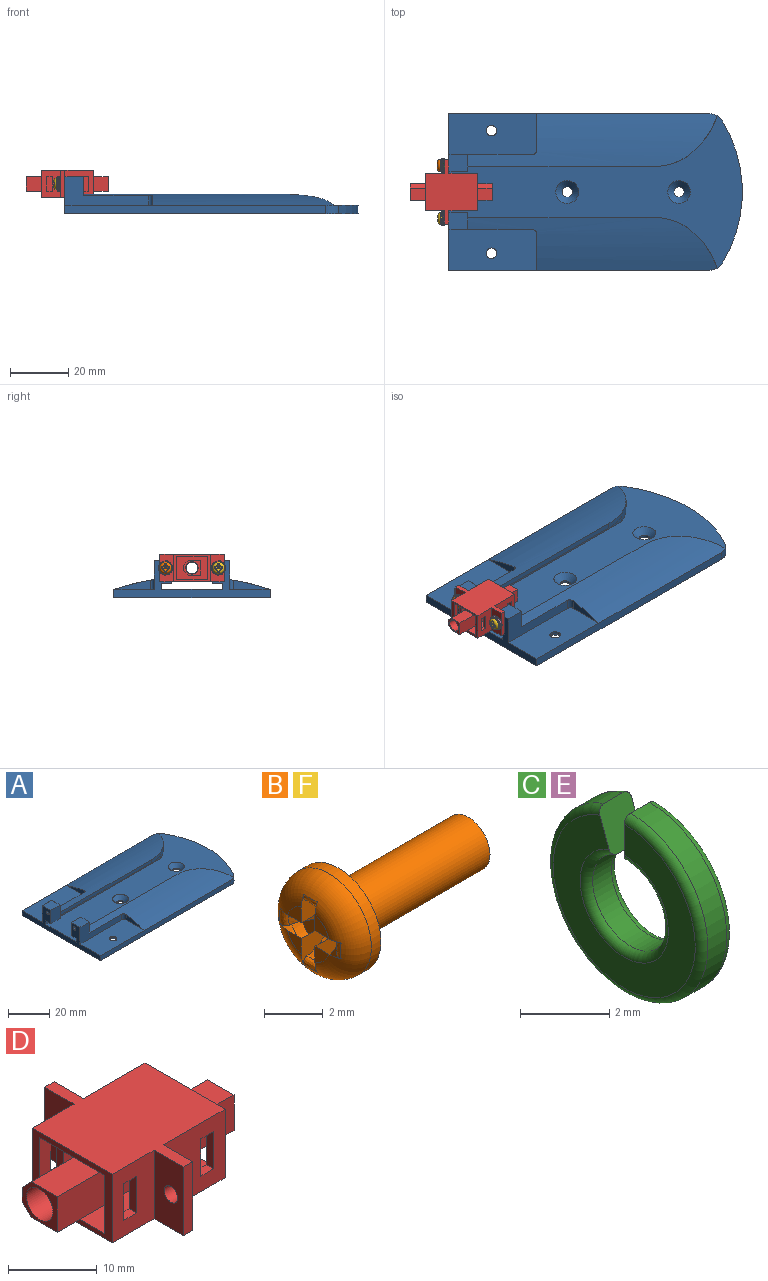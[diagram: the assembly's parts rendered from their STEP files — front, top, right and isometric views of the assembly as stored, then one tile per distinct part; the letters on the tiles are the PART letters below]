
ASSEMBLY  parts=6 mates=9
PART A: 44 faces, bbox 100.3x53.4x12.8 mm
  f0: plane 78.12x3.28mm, normal (0,0,-1), area 131mm2, adj f8,f10,f13,f15,f41,f43
  f1: cylinder r=83.84mm len=85.33mm, axis (-1,0,0), area 1130mm2, adj f2,f9,f11,f13,f16,f27,f28,f41
  f2: cylinder r=27.82mm len=12.7mm, axis (0,0,-1), area 31.5mm2, adj f1,f14,f28,f43
  f3: plane 78.12x3.28mm, normal (0,0,-1), area 131mm2, adj f8,f19,f22,f23,f40,f42
  f4: cylinder r=83.84mm len=85.33mm, axis (-1,0,0), area 1130mm2, adj f5,f18,f20,f22,f24,f26,f29,f40
  f5: cylinder r=27.82mm len=12.7mm, axis (0,0,-1), area 31.5mm2, adj f4,f14,f29,f42
  f6: plane 100.34x53.43mm, normal (0,0,-1), area 5099.9mm2, adj f7,f8,f9,f18,f28,f29,f32,f33
  f7: cylinder r=46.98mm len=48.6mm, axis (0,0,-1), area 146.6mm2, adj f6,f14,f28,f29
  f8: plane 53.43x12.75mm, normal (-1,0,0), area 249.5mm2, adj f0,f3,f6,f9,f10,f11,f12,f14
  f9: plane 89.28x2.87mm, normal (0,-1,0), area 256.2mm2, adj f1,f6,f8,f17,f28
  f10: plane 7.8x6.4mm, normal (0,1,0), area 49.9mm2, adj f0,f8,f12,f13
  f11: plane 28.56x9.88mm, normal (0,-1,0), area 138.1mm2, adj f1,f8,f12,f13,f17,f27
  f12: plane 6.4x5.8mm, normal (0,0,1), area 37.1mm2, adj f8,f10,f11,f13
  f13: plane 7.8x5.8mm, normal (1,0,0), area 36.4mm2, adj f0,f1,f10,f11,f12,f35,f41
  f14: plane 100.34x52.15mm, normal (0,0,1), area 2271.2mm2, adj f2,f5,f7,f8,f15,f23,f28,f29
  f15: plane 78.12x2.08mm, normal (0,1,0), area 162.5mm2, adj f0,f8,f14,f43
  f16: plane 12.36x3.13mm, normal (-1,0,0), area 21.4mm2, adj f1,f17,f27
  f17: plane 30.06x13.86mm, normal (0,0,1), area 405.8mm2, adj f8,f9,f11,f16,f27,f31
  f18: plane 89.28x2.87mm, normal (0,1,0), area 256.2mm2, adj f4,f6,f8,f25,f29
  f19: plane 7.8x6.4mm, normal (0,-1,0), area 49.9mm2, adj f3,f8,f21,f22
  f20: plane 28.56x9.88mm, normal (0,1,0), area 138.1mm2, adj f4,f8,f21,f22,f25,f26
  f21: plane 6.4x5.8mm, normal (0,0,1), area 37.1mm2, adj f8,f19,f20,f22
  f22: plane 7.8x5.8mm, normal (1,0,0), area 36.4mm2, adj f3,f4,f19,f20,f21,f34,f40
  f23: plane 78.12x2.08mm, normal (0,-1,0), area 162.5mm2, adj f3,f8,f14,f42
  f24: plane 12.36x3.13mm, normal (-1,0,0), area 21.4mm2, adj f4,f25,f26
  f25: plane 30.06x13.86mm, normal (0,0,1), area 405.8mm2, adj f8,f18,f20,f24,f26,f30
  f26: cylinder r=1.5mm len=3.38mm, axis (0,0,1), area 7.8mm2, adj f4,f20,f24,f25
  f27: cylinder r=1.5mm len=3.38mm, axis (0,0,1), area 7.8mm2, adj f1,f11,f16,f17
  f28: cylinder r=5mm len=4.28mm, axis (0,0,-1), area 14.9mm2, adj f1,f2,f6,f7,f9,f14
  f29: cylinder r=5mm len=4.28mm, axis (0,0,-1), area 14.9mm2, adj f4,f5,f6,f7,f14,f18
  f30: cylinder r=1.8mm len=3.6mm, axis (0,0,1), area 8.7mm2, adj f25,f38
  f31: cylinder r=1.8mm len=3.6mm, axis (0,0,1), area 8.7mm2, adj f17,f39
  f32: cylinder r=1.8mm len=3.6mm, axis (0,0,1), area 8.7mm2, adj f6,f36
  f33: cylinder r=1.8mm len=3.6mm, axis (0,0,1), area 8.7mm2, adj f6,f37
  f34: cylinder r=0.86mm len=6.4mm, axis (-1,0,0), area 34.8mm2, adj f8,f22
  f35: cylinder r=0.86mm len=6.4mm, axis (-1,0,0), area 34.8mm2, adj f8,f13
  f36: cone r=1.8mm half-angle=45deg, axis (0,0,1), area 53.2mm2, adj f14,f32
  f37: cone r=1.8mm half-angle=45deg, axis (0,0,1), area 53.2mm2, adj f14,f33
  f38: cone r=3.9mm half-angle=45deg, axis (0,0,-1), area 53.2mm2, adj f6,f30
  f39: cone r=1.8mm half-angle=45deg, axis (0,0,-1), area 53.2mm2, adj f6,f31
  f40: plane 63.91x1.83mm, normal (0,-1,0), area 117.1mm2, adj f3,f4,f22,f42
  f41: plane 63.91x1.83mm, normal (0,1,0), area 117.1mm2, adj f0,f1,f13,f43
  f42: cylinder r=20mm len=12.79mm, axis (0,0,-1), area 34.9mm2, adj f3,f4,f5,f14,f23,f40
  f43: cylinder r=20mm len=12.79mm, axis (0,0,-1), area 34.9mm2, adj f0,f1,f2,f14,f15,f41
PART B: 26 faces, bbox 7.8x4.5x4.5 mm
  f0: cylinder r=1.05mm len=6.25mm, axis (-1,0,0), area 41.2mm2, adj f10,f25
  f1: plane 0.67x0.67mm, normal (-1,0,0), area 0.3mm2, adj f2,f12,f16
  f2: torus R=1.04mm, axis (1,0,0), area 15.4mm2, adj f1,f3,f5,f6,f7,f8,f9,f12
  f3: plane 0.67x0.67mm, normal (-1,0,0), area 0.3mm2, adj f2,f13,f16
  f4: extruded ~1.16x0.86mm, area 1mm2, adj f5,f6,f15,f23
  f5: plane 1.43x1.17mm, normal (0,-1,0), area 0.9mm2, adj f2,f4,f7,f15,f23
  f6: plane 1.43x1.17mm, normal (0,1,0), area 0.9mm2, adj f2,f4,f9,f15,f23
  f7: plane 0.67x0.67mm, normal (-1,0,0), area 0.3mm2, adj f2,f5,f15
  f8: cylinder r=2.04mm len=4.09mm, axis (1,0,0), area 5.9mm2, adj f2,f10
  f9: plane 0.67x0.67mm, normal (-1,0,0), area 0.3mm2, adj f2,f6,f15
  f10: plane 4.09x4.09mm, normal (1,0,0), area 9.7mm2, adj f0,f8
  f11: extruded ~1.16x0.86mm, area 1mm2, adj f12,f13,f16,f24
  f12: plane 1.43x1.17mm, normal (0,-1,0), area 0.9mm2, adj f1,f2,f11,f16,f24
  f13: plane 1.43x1.17mm, normal (0,1,0), area 0.9mm2, adj f2,f3,f11,f16,f24
  f14: extruded ~2.37x1.21mm, area 2.2mm2, adj f15,f16,f17,f18,f19,f20,f21,f22
  f15: plane 2.96x1.49mm, normal (0,0,1), area 1.9mm2, adj f2,f4,f5,f6,f7,f9,f14,f21
  f16: plane 2.96x1.49mm, normal (0,0,-1), area 1.9mm2, adj f1,f2,f3,f11,f12,f13,f14,f21
  f17: plane 0.65x0.05mm, normal (0,1,0), area 0mm2, adj f14,f18
  f18: extruded ~0.65x0.33mm, area 0.1mm2, adj f14,f17
  f19: plane 0.65x0.05mm, normal (0,-1,0), area 0mm2, adj f14,f20
  f20: extruded ~0.65x0.33mm, area 0.1mm2, adj f14,f19
  f21: bspline ~0.97x0.3mm, area 0.2mm2, adj f2,f14,f15,f16
  f22: bspline ~0.97x0.3mm, area 0.2mm2, adj f2,f14,f15,f16
  f23: bspline ~0.97x0.3mm, area 0.2mm2, adj f2,f4,f5,f6
  f24: bspline ~0.97x0.3mm, area 0.2mm2, adj f2,f11,f12,f13
  f25: plane 2.1x2.1mm, normal (1,0,0), area 3.5mm2, adj f0
PART C: 10 faces, bbox 1x5.3x5.3 mm
  f0: cylinder r=2.45mm len=4.9mm, axis (-1,0,0), area 8.7mm2, adj f1,f7,f8,f9
  f1: torus R=2.25mm, axis (-1,0,0), area 4.4mm2, adj f0,f2,f8,f9
  f2: plane 4.5x4.5mm, normal (-1,0,0), area 9.2mm2, adj f1,f3,f8,f9
  f3: torus R=1.4mm, axis (-1,0,0), area 2.4mm2, adj f2,f4,f8,f9
  f4: cylinder r=1.2mm len=2.4mm, axis (-1,0,0), area 4.3mm2, adj f3,f5,f8,f9
  f5: torus R=1.4mm, axis (-1,0,0), area 2.4mm2, adj f4,f6,f8,f9
  f6: plane 4.5x4.5mm, normal (1,0,0), area 9.2mm2, adj f5,f7,f8,f9
  f7: torus R=2.25mm, axis (-1,0,0), area 4.4mm2, adj f0,f6,f8,f9
  f8: plane 1.17x1mm, normal (0,-0.94,0.34), area 1.2mm2, adj f0,f1,f2,f3,f4,f5,f6,f7
  f9: plane 1.25x1mm, normal (0,1,0), area 1.2mm2, adj f0,f1,f2,f3,f4,f5,f6,f7
PART D: 61 faces, bbox 28.1x22x9.4 mm
  f0: plane 10.39x8.04mm, normal (1,0,0), area 58.1mm2, adj f3,f4,f23,f24,f49,f50,f51,f53
  f1: plane 9.79x9.44mm, normal (0,1,0), area 81.9mm2, adj f9,f13,f14,f19,f45,f46,f47,f48
  f2: plane 9.79x9.44mm, normal (0,-1,0), area 81.9mm2, adj f9,f13,f14,f17,f41,f42,f43,f44
  f3: plane 8.25x8.04mm, normal (0,-1,0), area 55.8mm2, adj f0,f9,f23,f24,f45,f46,f47,f48
  f4: plane 8.25x8.04mm, normal (0,1,0), area 55.8mm2, adj f0,f9,f23,f24,f41,f42,f43,f44
  f5: plane 10.39x8.25mm, normal (0,0,-1), area 85.7mm2, adj f6,f8,f10,f25
  f6: plane 8.25x8.04mm, normal (0,-1,0), area 56mm2, adj f5,f7,f10,f25,f30,f31,f32,f33
  f7: plane 10.39x8.25mm, normal (0,0,1), area 85.7mm2, adj f6,f8,f10,f25
  f8: plane 8.25x8.04mm, normal (0,1,0), area 56mm2, adj f5,f7,f10,f25,f26,f27,f28,f29
  f9: plane 12.73x9.44mm, normal (1,0,0), area 36.6mm2, adj f1,f2,f3,f4,f13,f14,f23,f24
  f10: plane 12.73x9.44mm, normal (-1,0,0), area 36.6mm2, adj f5,f6,f7,f8,f11,f12,f13,f14
  f11: plane 9.44x6.64mm, normal (0,1,0), area 52.3mm2, adj f10,f13,f14,f18,f30,f31,f32,f33
  f12: plane 9.44x6.64mm, normal (0,-1,0), area 52.3mm2, adj f10,f13,f14,f16,f26,f27,f28,f29
  f13: plane 22.03x17.93mm, normal (0,0,1), area 242.2mm2, adj f1,f2,f9,f10,f11,f12,f15,f16
  f14: plane 22.03x17.93mm, normal (0,0,-1), area 242.2mm2, adj f1,f2,f9,f10,f11,f12,f15,f16
  f15: plane 9.44x1.5mm, normal (0,-1,0), area 14.2mm2, adj f13,f14,f16,f17
  f16: plane 9.44x4.65mm, normal (-1,0,0), area 40.3mm2, adj f12,f13,f14,f15,f22
  f17: plane 9.44x4.65mm, normal (1,0,0), area 40.3mm2, adj f2,f13,f14,f15,f22
  f18: plane 9.44x4.65mm, normal (-1,0,0), area 40.3mm2, adj f11,f13,f14,f20,f21
  f19: plane 9.44x4.65mm, normal (1,0,0), area 40.3mm2, adj f1,f13,f14,f20,f21
  f20: plane 9.44x1.5mm, normal (0,1,0), area 14.2mm2, adj f13,f14,f18,f19
  f21: cylinder r=1.07mm len=2.15mm, axis (-1,0,0), area 10.1mm2, adj f18,f19
  f22: cylinder r=1.07mm len=2.15mm, axis (-1,0,0), area 10.1mm2, adj f16,f17
  f23: plane 10.39x8.25mm, normal (0,0,-1), area 85.7mm2, adj f0,f3,f4,f9
  f24: plane 10.39x8.25mm, normal (0,0,1), area 85.7mm2, adj f0,f3,f4,f9
  f25: plane 10.39x8.04mm, normal (-1,0,0), area 58.1mm2, adj f5,f6,f7,f8,f34,f35,f36,f38
  f26: plane 5.04x1.17mm, normal (-1,0,0), area 5.9mm2, adj f8,f12,f27,f29
  f27: plane 2.05x1.17mm, normal (0,0,1), area 2.4mm2, adj f8,f12,f26,f28
  f28: plane 5.04x1.17mm, normal (1,0,0), area 5.9mm2, adj f8,f12,f27,f29
  f29: plane 2.05x1.17mm, normal (0,0,-1), area 2.4mm2, adj f8,f12,f26,f28
  f30: plane 2.05x1.17mm, normal (0,0,-1), area 2.4mm2, adj f6,f11,f31,f33
  f31: plane 5.04x1.17mm, normal (1,0,0), area 5.9mm2, adj f6,f11,f30,f32
  f32: plane 2.05x1.17mm, normal (0,0,1), area 2.4mm2, adj f6,f11,f31,f33
  f33: plane 5.04x1.17mm, normal (-1,0,0), area 5.9mm2, adj f6,f11,f30,f32
  f34: plane 13.43x4.14mm, normal (0,0,1), area 55.6mm2, adj f25,f38,f39,f59
  f35: plane 13.43x1.9mm, normal (0,1,0), area 25.5mm2, adj f25,f39,f59,f60
  f36: plane 13.43x4.14mm, normal (0,0,-1), area 55.6mm2, adj f25,f38,f39,f60
  f37: cylinder r=2.1mm len=13.43mm, axis (1,0,0), area 177.2mm2, adj f39,f40
  f38: plane 13.43x4.9mm, normal (0,-1,0), area 65.8mm2, adj f25,f34,f36,f39
  f39: plane 5.64x4.9mm, normal (-1,0,0), area 11.5mm2, adj f34,f35,f36,f37,f38,f59,f60
  f40: plane 4.2x4.2mm, normal (-1,0,0), area 1mm2, adj f37,f56
  f41: plane 2.05x1.17mm, normal (0,0,1), area 2.4mm2, adj f2,f4,f42,f44
  f42: plane 5.14x1.17mm, normal (1,0,0), area 6mm2, adj f2,f4,f41,f43
  f43: plane 2.05x1.17mm, normal (0,0,-1), area 2.4mm2, adj f2,f4,f42,f44
  f44: plane 5.14x1.17mm, normal (-1,0,0), area 6mm2, adj f2,f4,f41,f43
  f45: plane 5.14x1.17mm, normal (-1,0,0), area 6mm2, adj f1,f3,f46,f48
  f46: plane 2.05x1.17mm, normal (0,0,-1), area 2.4mm2, adj f1,f3,f45,f47
  f47: plane 5.14x1.17mm, normal (1,0,0), area 6mm2, adj f1,f3,f46,f48
  f48: plane 2.05x1.17mm, normal (0,0,1), area 2.4mm2, adj f1,f3,f45,f47
  f49: plane 13.22x4.14mm, normal (0,0,1), area 54.7mm2, adj f0,f53,f54,f57
  f50: plane 13.22x1.9mm, normal (0,1,0), area 25.1mm2, adj f0,f54,f57,f58
  f51: plane 13.22x4.14mm, normal (0,0,-1), area 54.7mm2, adj f0,f53,f54,f58
  f52: cylinder r=2.1mm len=13.22mm, axis (-1,0,0), area 174.4mm2, adj f54,f55
  f53: plane 13.22x4.9mm, normal (0,-1,0), area 64.8mm2, adj f0,f49,f51,f54
  f54: plane 5.64x4.9mm, normal (1,0,0), area 11.5mm2, adj f49,f50,f51,f52,f53,f57,f58
  f55: plane 4.2x4.2mm, normal (1,0,0), area 1mm2, adj f52,f56
  f56: cylinder r=2.02mm len=4.04mm, axis (1,0,0), area 18.2mm2, adj f40,f55
  f57: plane 13.22x1.5mm, normal (0,0.71,0.71), area 28mm2, adj f0,f49,f50,f54
  f58: plane 13.22x1.5mm, normal (0,0.71,-0.71), area 28mm2, adj f0,f50,f51,f54
  f59: plane 13.43x1.5mm, normal (0,0.71,0.71), area 28.5mm2, adj f25,f34,f35,f39
  f60: plane 13.43x1.5mm, normal (0,0.71,-0.71), area 28.5mm2, adj f25,f35,f36,f39
PART E: same geometry as C
PART F: same geometry as B
PLACE A t=(0.06,-34.61,-25.48)mm
PLACE B t=(-62.82,-21.7,-15.24)mm
PLACE C t=(-62.82,-21.7,-15.24)mm
PLACE D t=(-59.49,-30.76,-15.24)mm
PLACE E t=(-62.82,-39.82,-15.24)mm
PLACE F t=(-62.62,-39.82,-15.24)mm
MATE revolute F.f2 <-> E.f0  axis (1,0,0) through (-62.62,-39.82,-15.24)mm
MATE revolute C.f6 <-> D.f21  axis (1,0,0) through (-61.82,-21.22,-13.93)mm
MATE revolute D.f21 <-> A.f34  axis (-1,0,0) through (-61.07,-21.7,-15.24)mm
MATE revolute D.f22 <-> A.f35  axis (1,0,0) through (-60.32,-39.82,-15.24)mm
MATE revolute B.f2 <-> C.f0  axis (1,0,0) through (-62.82,-21.7,-15.24)mm
MATE parallel A.f8 <-> A.f34  axis (-1,0,0) through (-60.32,-20.42,-20.53)mm
MATE revolute C.f0 <-> D.f21  axis (1,0,0) through (-61.82,-21.7,-15.24)mm
MATE revolute E.f0 <-> D.f22  axis (1,0,0) through (-61.82,-39.82,-15.24)mm
MATE revolute D.f21 <-> A.f34  axis (1,0,0) through (-60.32,-21.7,-15.24)mm
